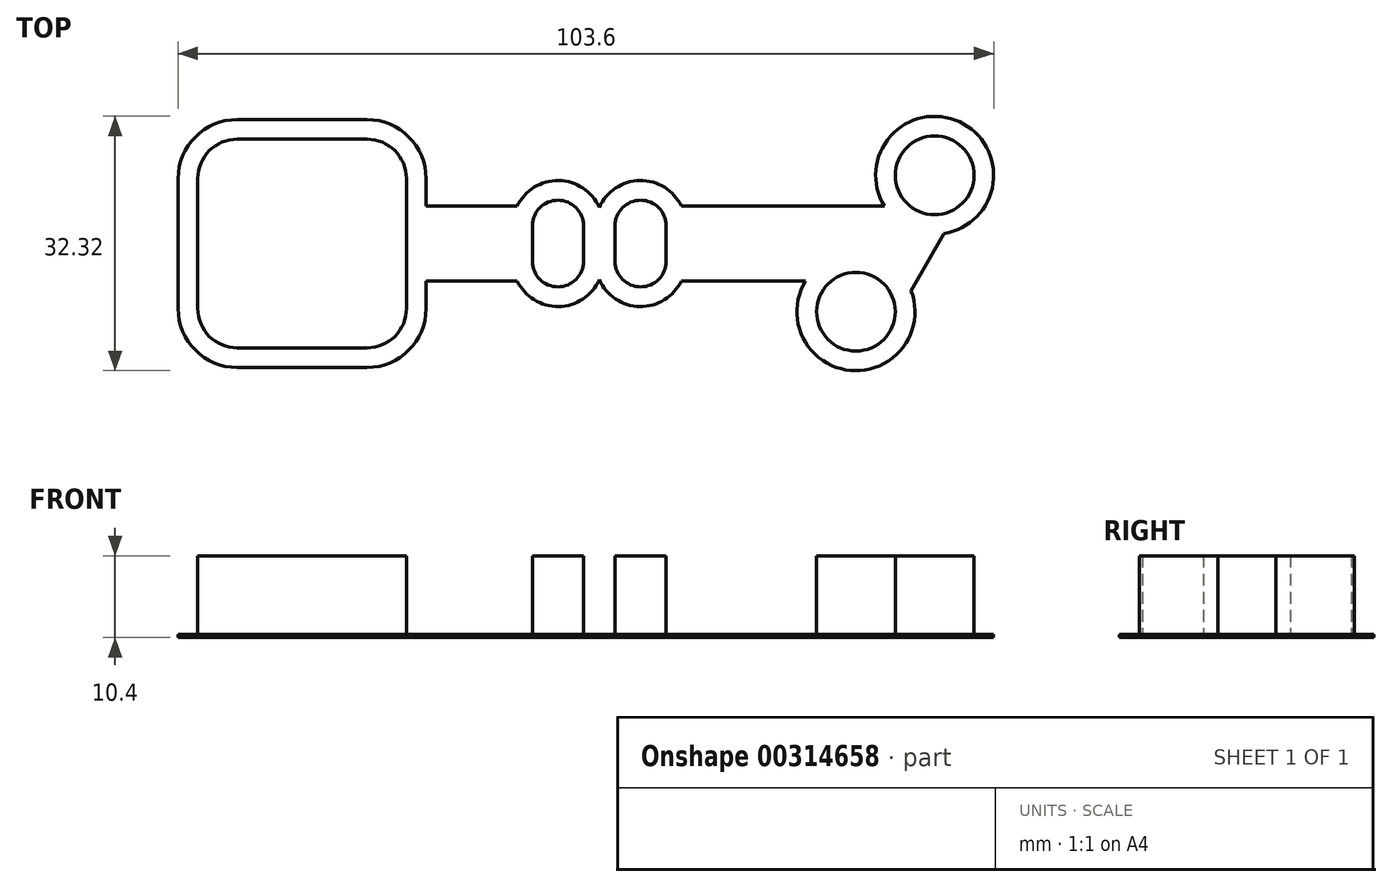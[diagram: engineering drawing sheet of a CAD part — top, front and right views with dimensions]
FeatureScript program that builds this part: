
annotation { "Feature Type Name" : "Feature", "Feature Type Description" : "" }
export const myFeature = defineFeature(function(context is Context, id is Id, definition is map)
    precondition{}
    {
        {
            var Q0;
            Q0=qCreatedBy(makeId("Top.planeOp"),FACE);
            var sketch = newSketch(context, id + "F0", { "sketchPlane" : qUnion([Q0])});
            skLineSegment(sketch, "E0.bottom", {"start": v(-8.25, 13.25) * mm, "end": v(8.25, 13.25) * mm});
            skLineSegment(sketch, "E0.top", {"start": v(-8.25, -13.25) * mm, "end": v(8.25, -13.25) * mm});
            skLineSegment(sketch, "E0.left", {"start": v(-13.25, 8.25) * mm, "end": v(-13.25, -8.25) * mm});
            skLineSegment(sketch, "E0.right", {"start": v(13.25, 8.25) * mm, "end": v(13.25, 2.25) * mm});
            skPoint(sketch, "E0.middle", {"position": v(0, 0) * mm});
            skCircle(sketch, "E1", {"center": v(0, 0) * mm, "radius": 4.5 * mm});
            skLineSegment(sketch, "E2", {"start": v(4.5, 13.25) * mm, "end": v(4.5, -13.25) * mm});
            skLineSegment(sketch, "E3", {"start": v(-4.5, 13.25) * mm, "end": v(-4.5, -13.25) * mm});
            skLineSegment(sketch, "E4", {"start": v(-13.25, 4.5) * mm, "end": v(13.25, 4.5) * mm});
            skLineSegment(sketch, "E5", {"start": v(-13.25, -4.5) * mm, "end": v(13.25, -4.5) * mm});
            skPoint(sketch, "E6.visualSharp", {"position": v(13.25, 13.25) * mm});
            skArc(sketch, "E6.filletArc", {"start": v(13.25, 8.25) * mm, "mid": v(11.79, 11.79) * mm, "end": v(8.25, 13.25) * mm});
            skPoint(sketch, "E7.visualSharp", {"position": v(-13.25, 13.25) * mm});
            skArc(sketch, "E7.filletArc", {"start": v(-8.25, 13.25) * mm, "mid": v(-11.79, 11.79) * mm, "end": v(-13.25, 8.25) * mm});
            skPoint(sketch, "E8.visualSharp", {"position": v(-13.25, -13.25) * mm});
            skArc(sketch, "E8.filletArc", {"start": v(-13.25, -8.25) * mm, "mid": v(-11.79, -11.79) * mm, "end": v(-8.25, -13.25) * mm});
            skPoint(sketch, "E9.visualSharp", {"position": v(13.25, -13.25) * mm});
            skArc(sketch, "E9.filletArc", {"start": v(8.25, -13.25) * mm, "mid": v(11.79, -11.79) * mm, "end": v(13.25, -8.25) * mm});
            skLineSegment(sketch, "E10", {"start": v(-40.8, 0) * mm, "end": v(144.75, 0) * mm, "construction": true});
            skPoint(sketch, "E10.startSnap0", {"position": v(-13.25, 0) * mm});
            skPoint(sketch, "E10.endSnap0", {"position": v(13.25, 0) * mm});
            skLineSegment(sketch, "E11", {"start": v(13.25, 2.25) * mm, "end": v(13.25, 2.25) * mm});
            skLineSegment(sketch, "E12", {"start": v(29.25, 2.25) * mm, "end": v(29.25, -2.25) * mm});
            skLineSegment(sketch, "E13", {"start": v(29.25, -2.25) * mm, "end": v(13.25, -2.25) * mm});
            skLineSegment(sketch, "E14.bottom", {"start": v(29.25, 2.25) * mm, "end": v(35.75, 2.25) * mm});
            skLineSegment(sketch, "E14.top", {"start": v(29.25, -2.25) * mm, "end": v(35.75, -2.25) * mm});
            skLineSegment(sketch, "E14.right", {"start": v(35.75, 2.25) * mm, "end": v(35.75, -2.25) * mm});
            skLineSegment(sketch, "E15.bottom", {"start": v(35.75, 2.25) * mm, "end": v(39.75, 2.25) * mm});
            skLineSegment(sketch, "E15.top", {"start": v(35.75, -2.25) * mm, "end": v(39.75, -2.25) * mm});
            skLineSegment(sketch, "E15.right", {"start": v(39.75, 2.25) * mm, "end": v(39.75, -2.25) * mm});
            skLineSegment(sketch, "E16.bottom", {"start": v(39.75, 2.25) * mm, "end": v(46.25, 2.25) * mm});
            skLineSegment(sketch, "E16.top", {"start": v(39.75, -2.25) * mm, "end": v(46.25, -2.25) * mm});
            skLineSegment(sketch, "E16.right", {"start": v(46.25, 2.25) * mm, "end": v(46.25, -2.25) * mm});
            skLineSegment(sketch, "E17", {"start": v(37.75, 18.32) * mm, "end": v(37.75, -19.52) * mm, "construction": true});
            skPoint(sketch, "E17.startSnap0", {"position": v(37.75, 2.25) * mm});
            skPoint(sketch, "E17.endSnap0", {"position": v(37.75, -2.25) * mm});
            skArc(sketch, "E18", {"start": v(29.25, 2.25) * mm, "mid": v(32.5, 5.5) * mm, "end": v(35.75, 2.25) * mm});
            skArc(sketch, "E19.MirrorCS", {"start": v(46.25, 2.25) * mm, "mid": v(43, 5.5) * mm, "end": v(39.75, 2.25) * mm});
            skArc(sketch, "E20.MirrorCS", {"start": v(46.25, -2.25) * mm, "mid": v(43, -5.5) * mm, "end": v(39.75, -2.25) * mm});
            skArc(sketch, "E21.MirrorCS", {"start": v(29.25, -2.25) * mm, "mid": v(32.5, -5.5) * mm, "end": v(35.75, -2.25) * mm});
            skLineSegment(sketch, "E22", {"start": v(46.25, 2.25) * mm, "end": v(74.05, 2.25) * mm});
            skLineSegment(sketch, "E23", {"start": v(80.35, 8.66) * mm, "end": v(70.35, -8.66) * mm, "construction": true});
            skLineSegment(sketch, "E24", {"start": v(76.17, 5.92) * mm, "end": v(76.17, 5.92) * mm});
            skLineSegment(sketch, "E25.MirrorCS", {"start": v(80.06, 3.67) * mm, "end": v(74.53, -5.92) * mm});
            skPoint(sketch, "E26", {"position": v(75.35, 0) * mm});
            skPoint(sketch, "E27", {"position": v(72.75, 0) * mm});
            skLineSegment(sketch, "E28.MirrorCS", {"start": v(46.25, -2.25) * mm, "end": v(71.45, -2.25) * mm});
            skPoint(sketch, "E29.orphan", {"position": v(72.75, -2.25) * mm});
            skPoint(sketch, "E30.orphan", {"position": v(72.75, 2.25) * mm});
            skLineSegment(sketch, "E31", {"start": v(13.25, 2.25) * mm, "end": v(29.25, 2.25) * mm});
            skLineSegment(sketch, "E32", {"start": v(13.25, -2.25) * mm, "end": v(13.25, -8.25) * mm});
            skLineSegment(sketch, "E33", {"start": v(13.25, 2.25) * mm, "end": v(13.25, -2.25) * mm});
            skLineSegment(sketch, "E34", {"start": v(13.25, -2.25) * mm, "end": v(13.25, -2.25) * mm});
            skLineSegment(sketch, "E35", {"start": v(71.45, -2.25) * mm, "end": v(71.45, -2.25) * mm});
            skLineSegment(sketch, "E36", {"start": v(74.05, 2.25) * mm, "end": v(71.45, -2.25) * mm});
            skLineSegment(sketch, "E37", {"start": v(71.45, -2.25) * mm, "end": v(70.63, -3.67) * mm});
            skLineSegment(sketch, "E38", {"start": v(74.05, 2.25) * mm, "end": v(74.05, 2.25) * mm});
            skLineSegment(sketch, "E39", {"start": v(76.17, 5.92) * mm, "end": v(74.05, 2.25) * mm});
            skArc(sketch, "E40", {"start": v(80.06, 3.67) * mm, "mid": v(82.85, 13) * mm, "end": v(76.17, 5.92) * mm});
            skArc(sketch, "E41", {"start": v(76.17, 5.92) * mm, "mid": v(77.85, 4.33) * mm, "end": v(80.06, 3.67) * mm});
            skArc(sketch, "E42", {"start": v(74.53, -5.92) * mm, "mid": v(72.85, -4.33) * mm, "end": v(70.63, -3.67) * mm});
            skArc(sketch, "E43", {"start": v(70.63, -3.67) * mm, "mid": v(67.85, -13) * mm, "end": v(74.53, -5.92) * mm});
            skLineSegment(sketch, "E44.0", {"start": v(15.75, 8.25) * mm, "end": v(15.75, 4.75) * mm});
            skLineSegment(sketch, "E44.1", {"start": v(15.75, 4.75) * mm, "end": v(27.32, 4.75) * mm});
            skArc(sketch, "E44.2", {"start": v(27.32, 4.75) * mm, "mid": v(32.59, 8) * mm, "end": v(37.75, 4.6) * mm});
            skArc(sketch, "E44.3", {"start": v(48.18, 4.75) * mm, "mid": v(42.91, 8) * mm, "end": v(37.75, 4.6) * mm});
            skLineSegment(sketch, "E44.4", {"start": v(48.18, 4.75) * mm, "end": v(73.95, 4.75) * mm});
            skArc(sketch, "E44.5", {"start": v(15.75, 8.25) * mm, "mid": v(13.55, 13.55) * mm, "end": v(8.25, 15.75) * mm});
            skArc(sketch, "E44.6", {"start": v(81.56, 1.26) * mm, "mid": v(83.47, 15.48) * mm, "end": v(73.95, 4.75) * mm});
            skLineSegment(sketch, "E44.7", {"start": v(81.56, 1.26) * mm, "end": v(77.36, -6) * mm});
            skArc(sketch, "E44.8", {"start": v(63.95, -4.75) * mm, "mid": v(69.65, -16.13) * mm, "end": v(77.36, -6) * mm});
            skLineSegment(sketch, "E44.9", {"start": v(48.18, -4.75) * mm, "end": v(63.95, -4.75) * mm});
            skArc(sketch, "E44.10", {"start": v(-15.75, -8.25) * mm, "mid": v(-13.55, -13.55) * mm, "end": v(-8.25, -15.75) * mm});
            skLineSegment(sketch, "E44.11", {"start": v(-15.75, 8.25) * mm, "end": v(-15.75, -8.25) * mm});
            skArc(sketch, "E44.12", {"start": v(-8.25, 15.75) * mm, "mid": v(-13.55, 13.55) * mm, "end": v(-15.75, 8.25) * mm});
            skLineSegment(sketch, "E44.13", {"start": v(-8.25, 15.75) * mm, "end": v(8.25, 15.75) * mm});
            skLineSegment(sketch, "E44.14", {"start": v(-8.25, -15.75) * mm, "end": v(8.25, -15.75) * mm});
            skArc(sketch, "E44.15", {"start": v(8.25, -15.75) * mm, "mid": v(13.55, -13.55) * mm, "end": v(15.75, -8.25) * mm});
            skLineSegment(sketch, "E44.16", {"start": v(15.75, -4.75) * mm, "end": v(15.75, -8.25) * mm});
            skLineSegment(sketch, "E44.17", {"start": v(27.32, -4.75) * mm, "end": v(15.75, -4.75) * mm});
            skArc(sketch, "E44.18", {"start": v(27.32, -4.75) * mm, "mid": v(32.59, -8) * mm, "end": v(37.75, -4.6) * mm});
            skArc(sketch, "E44.19", {"start": v(48.18, -4.75) * mm, "mid": v(42.91, -8) * mm, "end": v(37.75, -4.6) * mm});
            skSolve(sketch);
        }
        {
            var Q0;
            {var subQ0=sQuery(id+"F0.wireOp",EDGE,"E4");var subQ1=sQuery(id+"F0.wireOp",EDGE,"E1");var subQ2=makeQuery(id+"F0.imprint","INTERSECT",VERTEX,{"derivedFrom":[subQ1,subQ0]});Q0=makeQuery(id+"F0.imprint","IMPRINT",FACE,{"disambiguationData":[TD([[makeQuery(id+"F0.imprint","IMPRINT",EDGE,{"disambiguationData":[TD([[subQ2,1.0]])],"derivedFrom":subQ1}),-1.0]])]});}
            var Q1;
            {var subQ7=sQuery(id+"F0.wireOp",EDGE,"E8.filletArc");Q1=makeQuery(id+"F0.imprint","IMPRINT",FACE,{"disambiguationData":[TD([[makeQuery(id+"F0.imprint","IMPRINT",EDGE,{"derivedFrom":subQ7}),1.0]])]});}
            var Q2;
            Q2=makeQuery(id+"F0.imprint","IMPRINT",FACE,{"disambiguationData":[TD([[makeQuery(id+"F0.imprint","IMPRINT",EDGE,{"derivedFrom":sQuery(id+"F0.wireOp",EDGE,"E42")}),1.0]])]});
            var Q3;
            {var subQ0=sQuery(id+"F0.wireOp",EDGE,"E9.filletArc");Q3=makeQuery(id+"F0.imprint","IMPRINT",FACE,{"disambiguationData":[TD([[makeQuery(id+"F0.imprint","IMPRINT",EDGE,{"derivedFrom":subQ0}),1.0]])]});}
            var Q4;
            {var subQ4=sQuery(id+"F0.wireOp",EDGE,"E0.bottom");var subQ6=sQuery(id+"F0.wireOp",EDGE,"E2");var subQ7=makeQuery(id+"F0.imprint","INTERSECT",VERTEX,{"derivedFrom":[subQ4,subQ6]});Q4=makeQuery(id+"F0.imprint","IMPRINT",FACE,{"disambiguationData":[TD([[makeQuery(id+"F0.imprint","IMPRINT",EDGE,{"disambiguationData":[TD([[subQ7,1.0]])],"derivedFrom":subQ4}),-1.0]])]});}
            var Q5;
            {var subQ0=sQuery(id+"F0.wireOp",EDGE,"E6.filletArc");Q5=makeQuery(id+"F0.imprint","IMPRINT",FACE,{"disambiguationData":[TD([[makeQuery(id+"F0.imprint","IMPRINT",EDGE,{"derivedFrom":subQ0}),-1.0]])]});}
            var Q6;
            Q6=makeQuery(id+"F0.imprint","IMPRINT",FACE,{"disambiguationData":[TD([[makeQuery(id+"F0.imprint","IMPRINT",EDGE,{"derivedFrom":sQuery(id+"F0.wireOp",EDGE,"E14.bottom")}),1.0]])]});
            var Q7;
            {var subQ7=sQuery(id+"F0.wireOp",EDGE,"E7.filletArc");Q7=makeQuery(id+"F0.imprint","IMPRINT",FACE,{"disambiguationData":[TD([[makeQuery(id+"F0.imprint","IMPRINT",EDGE,{"derivedFrom":subQ7}),1.0]])]});}
            var Q8;
            Q8=makeQuery(id+"F0.imprint","IMPRINT",FACE,{"disambiguationData":[TD([[makeQuery(id+"F0.imprint","IMPRINT",EDGE,{"derivedFrom":sQuery(id+"F0.wireOp",EDGE,"E14.top")}),-1.0]])]});
            var Q9;
            Q9=makeQuery(id+"F0.imprint","IMPRINT",FACE,{"disambiguationData":[TD([[makeQuery(id+"F0.imprint","IMPRINT",EDGE,{"derivedFrom":sQuery(id+"F0.wireOp",EDGE,"E40")}),1.0]])]});
            var Q10;
            {var subQ7=sQuery(id+"F0.wireOp",EDGE,"E6.filletArc");Q10=makeQuery(id+"F0.imprint","IMPRINT",FACE,{"disambiguationData":[TD([[makeQuery(id+"F0.imprint","IMPRINT",EDGE,{"derivedFrom":subQ7}),1.0]])]});}
            var Q11;
            Q11=makeQuery(id+"F0.imprint","IMPRINT",FACE,{"disambiguationData":[TD([[makeQuery(id+"F0.imprint","IMPRINT",EDGE,{"derivedFrom":sQuery(id+"F0.wireOp",EDGE,"E14.bottom")}),-1.0]])]});
            var Q12;
            {var subQ8=sQuery(id+"F0.wireOp",EDGE,"E33");Q12=makeQuery(id+"F0.imprint","IMPRINT",FACE,{"disambiguationData":[TD([[makeQuery(id+"F0.imprint","IMPRINT",EDGE,{"derivedFrom":subQ8}),-1.0]])]});}
            var Q13;
            {var subQ0=sQuery(id+"F0.wireOp",EDGE,"E3");var subQ1=sQuery(id+"F0.wireOp",EDGE,"E1");var subQ2=makeQuery(id+"F0.imprint","INTERSECT",VERTEX,{"derivedFrom":[subQ1,subQ0]});Q13=makeQuery(id+"F0.imprint","IMPRINT",FACE,{"disambiguationData":[TD([[makeQuery(id+"F0.imprint","IMPRINT",EDGE,{"disambiguationData":[TD([[subQ2,-1.0]])],"derivedFrom":subQ1}),-1.0]])]});}
            var Q14;
            {var subQ0=sQuery(id+"F0.wireOp",EDGE,"E4");var subQ1=sQuery(id+"F0.wireOp",EDGE,"E1");var subQ2=makeQuery(id+"F0.imprint","INTERSECT",VERTEX,{"derivedFrom":[subQ1,subQ0]});Q14=makeQuery(id+"F0.imprint","IMPRINT",FACE,{"disambiguationData":[TD([[makeQuery(id+"F0.imprint","IMPRINT",EDGE,{"disambiguationData":[TD([[subQ2,-1.0]])],"derivedFrom":subQ1}),-1.0]])]});}
            var Q15;
            Q15=makeQuery(id+"F0.imprint","IMPRINT",FACE,{"disambiguationData":[TD([[makeQuery(id+"F0.imprint","IMPRINT",EDGE,{"derivedFrom":sQuery(id+"F0.wireOp",EDGE,"E16.bottom")}),1.0]])]});
            var Q16;
            Q16=makeQuery(id+"F0.imprint","IMPRINT",FACE,{"disambiguationData":[TD([[makeQuery(id+"F0.imprint","IMPRINT",EDGE,{"derivedFrom":sQuery(id+"F0.wireOp",EDGE,"E16.top")}),-1.0]])]});
            var Q17;
            Q17=makeQuery(id+"F0.imprint","IMPRINT",FACE,{"disambiguationData":[TD([[makeQuery(id+"F0.imprint","IMPRINT",EDGE,{"derivedFrom":sQuery(id+"F0.wireOp",EDGE,"E13")}),-1.0]])]});
            var Q18;
            Q18=makeQuery(id+"F0.imprint","IMPRINT",FACE,{"disambiguationData":[TD([[makeQuery(id+"F0.imprint","IMPRINT",EDGE,{"derivedFrom":sQuery(id+"F0.wireOp",EDGE,"E16.right")}),1.0]])]});
            var Q19;
            {var subQ0=sQuery(id+"F0.wireOp",EDGE,"E2");var subQ1=sQuery(id+"F0.wireOp",EDGE,"E1");var subQ2=makeQuery(id+"F0.imprint","INTERSECT",VERTEX,{"derivedFrom":[subQ1,subQ0]});Q19=makeQuery(id+"F0.imprint","IMPRINT",FACE,{"disambiguationData":[TD([[makeQuery(id+"F0.imprint","IMPRINT",EDGE,{"disambiguationData":[TD([[subQ2,1.0]])],"derivedFrom":subQ1}),-1.0]])]});}
            var Q20;
            Q20=makeQuery(id+"F0.imprint","IMPRINT",FACE,{"disambiguationData":[TD([[makeQuery(id+"F0.imprint","IMPRINT",EDGE,{"derivedFrom":sQuery(id+"F0.wireOp",EDGE,"E15.bottom")}),-1.0]])]});
            var Q21;
            {var subQ0=sQuery(id+"F0.wireOp",EDGE,"E4");var subQ1=sQuery(id+"F0.wireOp",EDGE,"E0.left");var subQ2=makeQuery(id+"F0.imprint","INTERSECT",VERTEX,{"derivedFrom":[subQ1,subQ0]});Q21=makeQuery(id+"F0.imprint","IMPRINT",FACE,{"disambiguationData":[TD([[makeQuery(id+"F0.imprint","IMPRINT",EDGE,{"disambiguationData":[TD([[subQ2,-1.0]])],"derivedFrom":subQ1}),1.0]])]});}
            var Q22;
            {var subQ0=sQuery(id+"F0.wireOp",EDGE,"E1");var subQ1=makeQuery(id+"F0.imprint","INTERSECT",VERTEX,{"derivedFrom":[subQ0,sQuery(id+"F0.wireOp",EDGE,"E4")]});Q22=makeQuery(id+"F0.imprint","IMPRINT",FACE,{"disambiguationData":[TD([[makeQuery(id+"F0.imprint","IMPRINT",EDGE,{"disambiguationData":[TD([[subQ1,1.0]])],"derivedFrom":subQ0}),1.0]])]});}
            var Q23;
            {var subQ1=sQuery(id+"F0.wireOp",EDGE,"E0.top");var subQ6=sQuery(id+"F0.wireOp",EDGE,"E2");var subQ7=makeQuery(id+"F0.imprint","INTERSECT",VERTEX,{"derivedFrom":[subQ1,subQ6]});Q23=makeQuery(id+"F0.imprint","IMPRINT",FACE,{"disambiguationData":[TD([[makeQuery(id+"F0.imprint","IMPRINT",EDGE,{"disambiguationData":[TD([[subQ7,1.0]])],"derivedFrom":subQ1}),1.0]])]});}
            var Q24;
            Q24=makeQuery(id+"F0.imprint","IMPRINT",FACE,{"disambiguationData":[TD([[makeQuery(id+"F0.imprint","IMPRINT",EDGE,{"derivedFrom":sQuery(id+"F0.wireOp",EDGE,"E25.MirrorCS")}),-1.0]])]});
            var Q25;
            Q25=makeQuery(id+"F0.imprint","IMPRINT",FACE,{"disambiguationData":[TD([[makeQuery(id+"F0.imprint","IMPRINT",EDGE,{"derivedFrom":sQuery(id+"F0.wireOp",EDGE,"E16.bottom")}),-1.0]])]});
            extrude(context, id + "F1", {"entities" : qUnion([Q0, Q1, Q2, Q3, Q4, Q5, Q6, Q7, Q8, Q9, Q10, Q11, Q12, Q13, Q14, Q15, Q16, Q17, Q18, Q19, Q20, Q21, Q22, Q23, Q24, Q25]), "depth" : 0.4 * mm});
        }
        {
            var Q0;
            Q0=makeQuery(id+"F1.opExtrude","CAP_FACE",FACE,{"disambiguationData":[OSD([sQuery(id+"F0.wireOp",EDGE,"E44.0"),sQuery(id+"F0.wireOp",EDGE,"E44.1"),sQuery(id+"F0.wireOp",EDGE,"E44.2"),sQuery(id+"F0.wireOp",EDGE,"E44.3"),sQuery(id+"F0.wireOp",EDGE,"E44.4"),sQuery(id+"F0.wireOp",EDGE,"E44.5"),sQuery(id+"F0.wireOp",EDGE,"E44.6"),sQuery(id+"F0.wireOp",EDGE,"E44.7"),sQuery(id+"F0.wireOp",EDGE,"E44.8"),sQuery(id+"F0.wireOp",EDGE,"E44.9"),sQuery(id+"F0.wireOp",EDGE,"E44.10"),sQuery(id+"F0.wireOp",EDGE,"E44.11"),sQuery(id+"F0.wireOp",EDGE,"E44.12"),sQuery(id+"F0.wireOp",EDGE,"E44.13"),sQuery(id+"F0.wireOp",EDGE,"E44.14"),sQuery(id+"F0.wireOp",EDGE,"E44.15"),sQuery(id+"F0.wireOp",EDGE,"E44.16"),sQuery(id+"F0.wireOp",EDGE,"E44.17"),sQuery(id+"F0.wireOp",EDGE,"E44.18"),sQuery(id+"F0.wireOp",EDGE,"E44.19")])],"isStart":false});
            var sketch = newSketch(context, id + "F2", { "sketchPlane" : qUnion([Q0])});
            skLineSegment(sketch, "E45.0", {"start": v(-8.25, 13.25) * mm, "end": v(8.25, 13.25) * mm});
            skLineSegment(sketch, "E45.1", {"start": v(-8.25, -13.25) * mm, "end": v(8.25, -13.25) * mm});
            skLineSegment(sketch, "E45.2", {"start": v(-13.25, 8.25) * mm, "end": v(-13.25, -8.25) * mm});
            skLineSegment(sketch, "E45.3", {"start": v(13.25, 8.25) * mm, "end": v(13.25, 2.25) * mm});
            skPoint(sketch, "E45.4", {"position": v(0, 0) * mm});
            skCircle(sketch, "E45.5", {"center": v(0, 0) * mm, "radius": 4.5 * mm});
            skLineSegment(sketch, "E45.6", {"start": v(4.5, 13.25) * mm, "end": v(4.5, -13.25) * mm});
            skLineSegment(sketch, "E45.7", {"start": v(-4.5, 13.25) * mm, "end": v(-4.5, -13.25) * mm});
            skLineSegment(sketch, "E45.8", {"start": v(-13.25, 4.5) * mm, "end": v(13.25, 4.5) * mm});
            skLineSegment(sketch, "E45.9", {"start": v(-13.25, -4.5) * mm, "end": v(13.25, -4.5) * mm});
            skPoint(sketch, "E45.10", {"position": v(13.25, 13.25) * mm});
            skArc(sketch, "E45.11", {"start": v(13.25, 8.25) * mm, "mid": v(11.79, 11.79) * mm, "end": v(8.25, 13.25) * mm});
            skPoint(sketch, "E45.12", {"position": v(-13.25, 13.25) * mm});
            skArc(sketch, "E45.13", {"start": v(-8.25, 13.25) * mm, "mid": v(-11.79, 11.79) * mm, "end": v(-13.25, 8.25) * mm});
            skPoint(sketch, "E45.14", {"position": v(-13.25, -13.25) * mm});
            skArc(sketch, "E45.15", {"start": v(-13.25, -8.25) * mm, "mid": v(-11.79, -11.79) * mm, "end": v(-8.25, -13.25) * mm});
            skPoint(sketch, "E45.16", {"position": v(13.25, -13.25) * mm});
            skArc(sketch, "E45.17", {"start": v(8.25, -13.25) * mm, "mid": v(11.79, -11.79) * mm, "end": v(13.25, -8.25) * mm});
            skPoint(sketch, "E45.19", {"position": v(-13.25, 0) * mm});
            skPoint(sketch, "E45.20", {"position": v(13.25, 0) * mm});
            skPoint(sketch, "E45.21", {"position": v(13.25, 2.25) * mm});
            skLineSegment(sketch, "E45.22", {"start": v(29.25, 2.25) * mm, "end": v(29.25, -2.25) * mm});
            skLineSegment(sketch, "E45.23", {"start": v(29.25, -2.25) * mm, "end": v(13.25, -2.25) * mm});
            skLineSegment(sketch, "E45.24", {"start": v(29.25, 2.25) * mm, "end": v(35.75, 2.25) * mm});
            skLineSegment(sketch, "E45.25", {"start": v(29.25, -2.25) * mm, "end": v(35.75, -2.25) * mm});
            skLineSegment(sketch, "E45.26", {"start": v(29.25, 2.25) * mm, "end": v(29.25, -2.25) * mm});
            skLineSegment(sketch, "E45.27", {"start": v(35.75, 2.25) * mm, "end": v(35.75, -2.25) * mm});
            skLineSegment(sketch, "E45.28", {"start": v(35.75, 2.25) * mm, "end": v(39.75, 2.25) * mm});
            skLineSegment(sketch, "E45.29", {"start": v(35.75, -2.25) * mm, "end": v(39.75, -2.25) * mm});
            skLineSegment(sketch, "E45.30", {"start": v(35.75, 2.25) * mm, "end": v(35.75, -2.25) * mm});
            skLineSegment(sketch, "E45.31", {"start": v(39.75, 2.25) * mm, "end": v(39.75, -2.25) * mm});
            skLineSegment(sketch, "E45.32", {"start": v(39.75, 2.25) * mm, "end": v(46.25, 2.25) * mm});
            skLineSegment(sketch, "E45.33", {"start": v(39.75, -2.25) * mm, "end": v(46.25, -2.25) * mm});
            skLineSegment(sketch, "E45.34", {"start": v(39.75, 2.25) * mm, "end": v(39.75, -2.25) * mm});
            skLineSegment(sketch, "E45.35", {"start": v(46.25, 2.25) * mm, "end": v(46.25, -2.25) * mm});
            skPoint(sketch, "E45.37", {"position": v(37.75, 2.25) * mm});
            skPoint(sketch, "E45.38", {"position": v(37.75, -2.25) * mm});
            skArc(sketch, "E45.39", {"start": v(29.25, 2.25) * mm, "mid": v(32.5, 5.5) * mm, "end": v(35.75, 2.25) * mm});
            skArc(sketch, "E45.40", {"start": v(46.25, 2.25) * mm, "mid": v(43, 5.5) * mm, "end": v(39.75, 2.25) * mm});
            skArc(sketch, "E45.41", {"start": v(46.25, -2.25) * mm, "mid": v(43, -5.5) * mm, "end": v(39.75, -2.25) * mm});
            skArc(sketch, "E45.42", {"start": v(29.25, -2.25) * mm, "mid": v(32.5, -5.5) * mm, "end": v(35.75, -2.25) * mm});
            skLineSegment(sketch, "E45.43", {"start": v(46.25, 2.25) * mm, "end": v(74.05, 2.25) * mm});
            skLineSegment(sketch, "E45.44", {"start": v(80.35, 8.66) * mm, "end": v(70.35, -8.66) * mm});
            skPoint(sketch, "E45.45", {"position": v(76.17, 5.92) * mm});
            skLineSegment(sketch, "E45.46", {"start": v(80.06, 3.67) * mm, "end": v(74.53, -5.92) * mm});
            skPoint(sketch, "E45.47", {"position": v(75.35, 0) * mm});
            skPoint(sketch, "E45.48", {"position": v(72.75, 0) * mm});
            skLineSegment(sketch, "E45.49", {"start": v(46.25, -2.25) * mm, "end": v(71.45, -2.25) * mm});
            skPoint(sketch, "E45.50", {"position": v(72.75, -2.25) * mm});
            skPoint(sketch, "E45.51", {"position": v(72.75, 2.25) * mm});
            skLineSegment(sketch, "E45.52", {"start": v(13.25, 2.25) * mm, "end": v(29.25, 2.25) * mm});
            skLineSegment(sketch, "E45.53", {"start": v(13.25, -2.25) * mm, "end": v(13.25, -8.25) * mm});
            skLineSegment(sketch, "E45.54", {"start": v(13.25, 2.25) * mm, "end": v(13.25, -2.25) * mm});
            skPoint(sketch, "E45.55", {"position": v(13.25, -2.25) * mm});
            skPoint(sketch, "E45.56", {"position": v(71.45, -2.25) * mm});
            skLineSegment(sketch, "E45.57", {"start": v(74.05, 2.25) * mm, "end": v(71.45, -2.25) * mm});
            skLineSegment(sketch, "E45.58", {"start": v(71.45, -2.25) * mm, "end": v(70.63, -3.67) * mm});
            skPoint(sketch, "E45.59", {"position": v(74.05, 2.25) * mm});
            skLineSegment(sketch, "E45.60", {"start": v(76.17, 5.92) * mm, "end": v(74.05, 2.25) * mm});
            skArc(sketch, "E45.61", {"start": v(80.06, 3.67) * mm, "mid": v(82.85, 13) * mm, "end": v(76.17, 5.92) * mm});
            skArc(sketch, "E45.62", {"start": v(76.17, 5.92) * mm, "mid": v(77.85, 4.33) * mm, "end": v(80.06, 3.67) * mm});
            skArc(sketch, "E45.63", {"start": v(74.53, -5.92) * mm, "mid": v(72.85, -4.33) * mm, "end": v(70.63, -3.67) * mm});
            skArc(sketch, "E45.64", {"start": v(70.63, -3.67) * mm, "mid": v(67.85, -13) * mm, "end": v(74.53, -5.92) * mm});
            skLineSegment(sketch, "E45.65", {"start": v(15.75, 8.25) * mm, "end": v(15.75, 4.75) * mm});
            skLineSegment(sketch, "E45.66", {"start": v(15.75, 4.75) * mm, "end": v(27.32, 4.75) * mm});
            skArc(sketch, "E45.67", {"start": v(27.32, 4.75) * mm, "mid": v(32.59, 8) * mm, "end": v(37.75, 4.6) * mm});
            skArc(sketch, "E45.68", {"start": v(48.18, 4.75) * mm, "mid": v(42.91, 8) * mm, "end": v(37.75, 4.6) * mm});
            skLineSegment(sketch, "E45.69", {"start": v(48.18, 4.75) * mm, "end": v(73.95, 4.75) * mm});
            skArc(sketch, "E45.70", {"start": v(15.75, 8.25) * mm, "mid": v(13.55, 13.55) * mm, "end": v(8.25, 15.75) * mm});
            skArc(sketch, "E45.71", {"start": v(81.56, 1.26) * mm, "mid": v(83.47, 15.48) * mm, "end": v(73.95, 4.75) * mm});
            skLineSegment(sketch, "E45.72", {"start": v(81.56, 1.26) * mm, "end": v(77.36, -6) * mm});
            skArc(sketch, "E45.73", {"start": v(63.95, -4.75) * mm, "mid": v(69.65, -16.13) * mm, "end": v(77.36, -6) * mm});
            skLineSegment(sketch, "E45.74", {"start": v(48.18, -4.75) * mm, "end": v(63.95, -4.75) * mm});
            skArc(sketch, "E45.75", {"start": v(-15.75, -8.25) * mm, "mid": v(-13.55, -13.55) * mm, "end": v(-8.25, -15.75) * mm});
            skLineSegment(sketch, "E45.76", {"start": v(-15.75, 8.25) * mm, "end": v(-15.75, -8.25) * mm});
            skArc(sketch, "E45.77", {"start": v(-8.25, 15.75) * mm, "mid": v(-13.55, 13.55) * mm, "end": v(-15.75, 8.25) * mm});
            skLineSegment(sketch, "E45.78", {"start": v(-8.25, 15.75) * mm, "end": v(8.25, 15.75) * mm});
            skLineSegment(sketch, "E45.79", {"start": v(-8.25, -15.75) * mm, "end": v(8.25, -15.75) * mm});
            skArc(sketch, "E45.80", {"start": v(8.25, -15.75) * mm, "mid": v(13.55, -13.55) * mm, "end": v(15.75, -8.25) * mm});
            skLineSegment(sketch, "E45.81", {"start": v(15.75, -4.75) * mm, "end": v(15.75, -8.25) * mm});
            skLineSegment(sketch, "E45.82", {"start": v(27.32, -4.75) * mm, "end": v(15.75, -4.75) * mm});
            skArc(sketch, "E45.83", {"start": v(27.32, -4.75) * mm, "mid": v(32.59, -8) * mm, "end": v(37.75, -4.6) * mm});
            skArc(sketch, "E45.84", {"start": v(48.18, -4.75) * mm, "mid": v(42.91, -8) * mm, "end": v(37.75, -4.6) * mm});
            skSolve(sketch);
        }
        {
            var Q0;
            {var subQ7=sQuery(id+"F2.wireOp",EDGE,"E45.11");Q0=makeQuery(id+"F2.imprint","IMPRINT",FACE,{"disambiguationData":[TD([[makeQuery(id+"F2.imprint","IMPRINT",EDGE,{"derivedFrom":subQ7}),1.0]])]});}
            var Q1;
            {var subQ8=sQuery(id+"F2.wireOp",EDGE,"E45.54");Q1=makeQuery(id+"F2.imprint","IMPRINT",FACE,{"disambiguationData":[TD([[makeQuery(id+"F2.imprint","IMPRINT",EDGE,{"derivedFrom":subQ8}),-1.0]])]});}
            var Q2;
            {var subQ0=sQuery(id+"F2.wireOp",EDGE,"E45.8");var subQ1=sQuery(id+"F2.wireOp",EDGE,"E45.5");var subQ2=makeQuery(id+"F2.imprint","INTERSECT",VERTEX,{"derivedFrom":[subQ1,subQ0]});Q2=makeQuery(id+"F2.imprint","IMPRINT",FACE,{"disambiguationData":[TD([[makeQuery(id+"F2.imprint","IMPRINT",EDGE,{"disambiguationData":[TD([[subQ2,1.0]])],"derivedFrom":subQ1}),-1.0]])]});}
            var Q3;
            {var subQ0=sQuery(id+"F2.wireOp",EDGE,"E45.5");var subQ1=makeQuery(id+"F2.imprint","INTERSECT",VERTEX,{"derivedFrom":[subQ0,sQuery(id+"F2.wireOp",EDGE,"E45.8")]});Q3=makeQuery(id+"F2.imprint","IMPRINT",FACE,{"disambiguationData":[TD([[makeQuery(id+"F2.imprint","IMPRINT",EDGE,{"disambiguationData":[TD([[subQ1,1.0]])],"derivedFrom":subQ0}),1.0]])]});}
            var Q4;
            {var subQ0=sQuery(id+"F2.wireOp",EDGE,"E45.8");var subQ1=sQuery(id+"F2.wireOp",EDGE,"E45.5");var subQ2=makeQuery(id+"F2.imprint","INTERSECT",VERTEX,{"derivedFrom":[subQ1,subQ0]});Q4=makeQuery(id+"F2.imprint","IMPRINT",FACE,{"disambiguationData":[TD([[makeQuery(id+"F2.imprint","IMPRINT",EDGE,{"disambiguationData":[TD([[subQ2,-1.0]])],"derivedFrom":subQ1}),-1.0]])]});}
            var Q5;
            {var subQ1=sQuery(id+"F2.wireOp",EDGE,"E45.1");var subQ6=sQuery(id+"F2.wireOp",EDGE,"E45.6");var subQ7=makeQuery(id+"F2.imprint","INTERSECT",VERTEX,{"derivedFrom":[subQ1,subQ6]});Q5=makeQuery(id+"F2.imprint","IMPRINT",FACE,{"disambiguationData":[TD([[makeQuery(id+"F2.imprint","IMPRINT",EDGE,{"disambiguationData":[TD([[subQ7,1.0]])],"derivedFrom":subQ1}),1.0]])]});}
            var Q6;
            {var subQ0=sQuery(id+"F2.wireOp",EDGE,"E45.7");var subQ1=sQuery(id+"F2.wireOp",EDGE,"E45.5");var subQ2=makeQuery(id+"F2.imprint","INTERSECT",VERTEX,{"derivedFrom":[subQ1,subQ0]});Q6=makeQuery(id+"F2.imprint","IMPRINT",FACE,{"disambiguationData":[TD([[makeQuery(id+"F2.imprint","IMPRINT",EDGE,{"disambiguationData":[TD([[subQ2,-1.0]])],"derivedFrom":subQ1}),-1.0]])]});}
            var Q7;
            {var subQ0=sQuery(id+"F2.wireOp",EDGE,"E45.6");var subQ1=sQuery(id+"F2.wireOp",EDGE,"E45.5");var subQ2=makeQuery(id+"F2.imprint","INTERSECT",VERTEX,{"derivedFrom":[subQ1,subQ0]});Q7=makeQuery(id+"F2.imprint","IMPRINT",FACE,{"disambiguationData":[TD([[makeQuery(id+"F2.imprint","IMPRINT",EDGE,{"disambiguationData":[TD([[subQ2,1.0]])],"derivedFrom":subQ1}),-1.0]])]});}
            var Q8;
            {var subQ0=sQuery(id+"F2.wireOp",EDGE,"E45.17");Q8=makeQuery(id+"F2.imprint","IMPRINT",FACE,{"disambiguationData":[TD([[makeQuery(id+"F2.imprint","IMPRINT",EDGE,{"derivedFrom":subQ0}),1.0]])]});}
            var Q9;
            {var subQ4=sQuery(id+"F2.wireOp",EDGE,"E45.0");var subQ6=sQuery(id+"F2.wireOp",EDGE,"E45.6");var subQ7=makeQuery(id+"F2.imprint","INTERSECT",VERTEX,{"derivedFrom":[subQ4,subQ6]});Q9=makeQuery(id+"F2.imprint","IMPRINT",FACE,{"disambiguationData":[TD([[makeQuery(id+"F2.imprint","IMPRINT",EDGE,{"disambiguationData":[TD([[subQ7,1.0]])],"derivedFrom":subQ4}),-1.0]])]});}
            var Q10;
            {var subQ7=sQuery(id+"F2.wireOp",EDGE,"E45.13");Q10=makeQuery(id+"F2.imprint","IMPRINT",FACE,{"disambiguationData":[TD([[makeQuery(id+"F2.imprint","IMPRINT",EDGE,{"derivedFrom":subQ7}),1.0]])]});}
            var Q11;
            {var subQ0=sQuery(id+"F2.wireOp",EDGE,"E45.8");var subQ1=sQuery(id+"F2.wireOp",EDGE,"E45.2");var subQ2=makeQuery(id+"F2.imprint","INTERSECT",VERTEX,{"derivedFrom":[subQ1,subQ0]});Q11=makeQuery(id+"F2.imprint","IMPRINT",FACE,{"disambiguationData":[TD([[makeQuery(id+"F2.imprint","IMPRINT",EDGE,{"disambiguationData":[TD([[subQ2,-1.0]])],"derivedFrom":subQ1}),1.0]])]});}
            var Q12;
            {var subQ7=sQuery(id+"F2.wireOp",EDGE,"E45.15");Q12=makeQuery(id+"F2.imprint","IMPRINT",FACE,{"disambiguationData":[TD([[makeQuery(id+"F2.imprint","IMPRINT",EDGE,{"derivedFrom":subQ7}),1.0]])]});}
            var Q13;
            Q13=makeQuery(id+"F2.imprint","IMPRINT",FACE,{"disambiguationData":[TD([[makeQuery(id+"F2.imprint","IMPRINT",EDGE,{"derivedFrom":sQuery(id+"F2.wireOp",EDGE,"E45.24")}),1.0]])]});
            var Q14;
            Q14=makeQuery(id+"F2.imprint","IMPRINT",FACE,{"disambiguationData":[TD([[makeQuery(id+"F2.imprint","IMPRINT",EDGE,{"derivedFrom":sQuery(id+"F2.wireOp",EDGE,"E45.24")}),-1.0]])]});
            var Q15;
            Q15=makeQuery(id+"F2.imprint","IMPRINT",FACE,{"disambiguationData":[TD([[makeQuery(id+"F2.imprint","IMPRINT",EDGE,{"derivedFrom":sQuery(id+"F2.wireOp",EDGE,"E45.25")}),-1.0]])]});
            var Q16;
            Q16=makeQuery(id+"F2.imprint","IMPRINT",FACE,{"disambiguationData":[TD([[makeQuery(id+"F2.imprint","IMPRINT",EDGE,{"derivedFrom":sQuery(id+"F2.wireOp",EDGE,"E45.33")}),-1.0]])]});
            var Q17;
            Q17=makeQuery(id+"F2.imprint","IMPRINT",FACE,{"disambiguationData":[TD([[makeQuery(id+"F2.imprint","IMPRINT",EDGE,{"derivedFrom":sQuery(id+"F2.wireOp",EDGE,"E45.32")}),-1.0]])]});
            var Q18;
            Q18=makeQuery(id+"F2.imprint","IMPRINT",FACE,{"disambiguationData":[TD([[makeQuery(id+"F2.imprint","IMPRINT",EDGE,{"derivedFrom":sQuery(id+"F2.wireOp",EDGE,"E45.32")}),1.0]])]});
            var Q19;
            {var subQ0=sQuery(id+"F2.wireOp",EDGE,"E45.64");Q19=makeQuery(id+"F2.imprint","IMPRINT",FACE,{"disambiguationData":[TD([[makeQuery(id+"F2.imprint","IMPRINT",EDGE,{"derivedFrom":subQ0}),1.0]])]});}
            var Q20;
            {var subQ0=sQuery(id+"F2.wireOp",EDGE,"E45.61");Q20=makeQuery(id+"F2.imprint","IMPRINT",FACE,{"disambiguationData":[TD([[makeQuery(id+"F2.imprint","IMPRINT",EDGE,{"derivedFrom":subQ0}),1.0]])]});}
            extrude(context, id + "F3", {"entities" : qUnion([Q0, Q1, Q2, Q3, Q4, Q5, Q6, Q7, Q8, Q9, Q10, Q11, Q12, Q13, Q14, Q15, Q16, Q17, Q18, Q19, Q20]), "operationType" : NewBodyOperationType.ADD, "depth" : 10 * mm});
        }
    });
